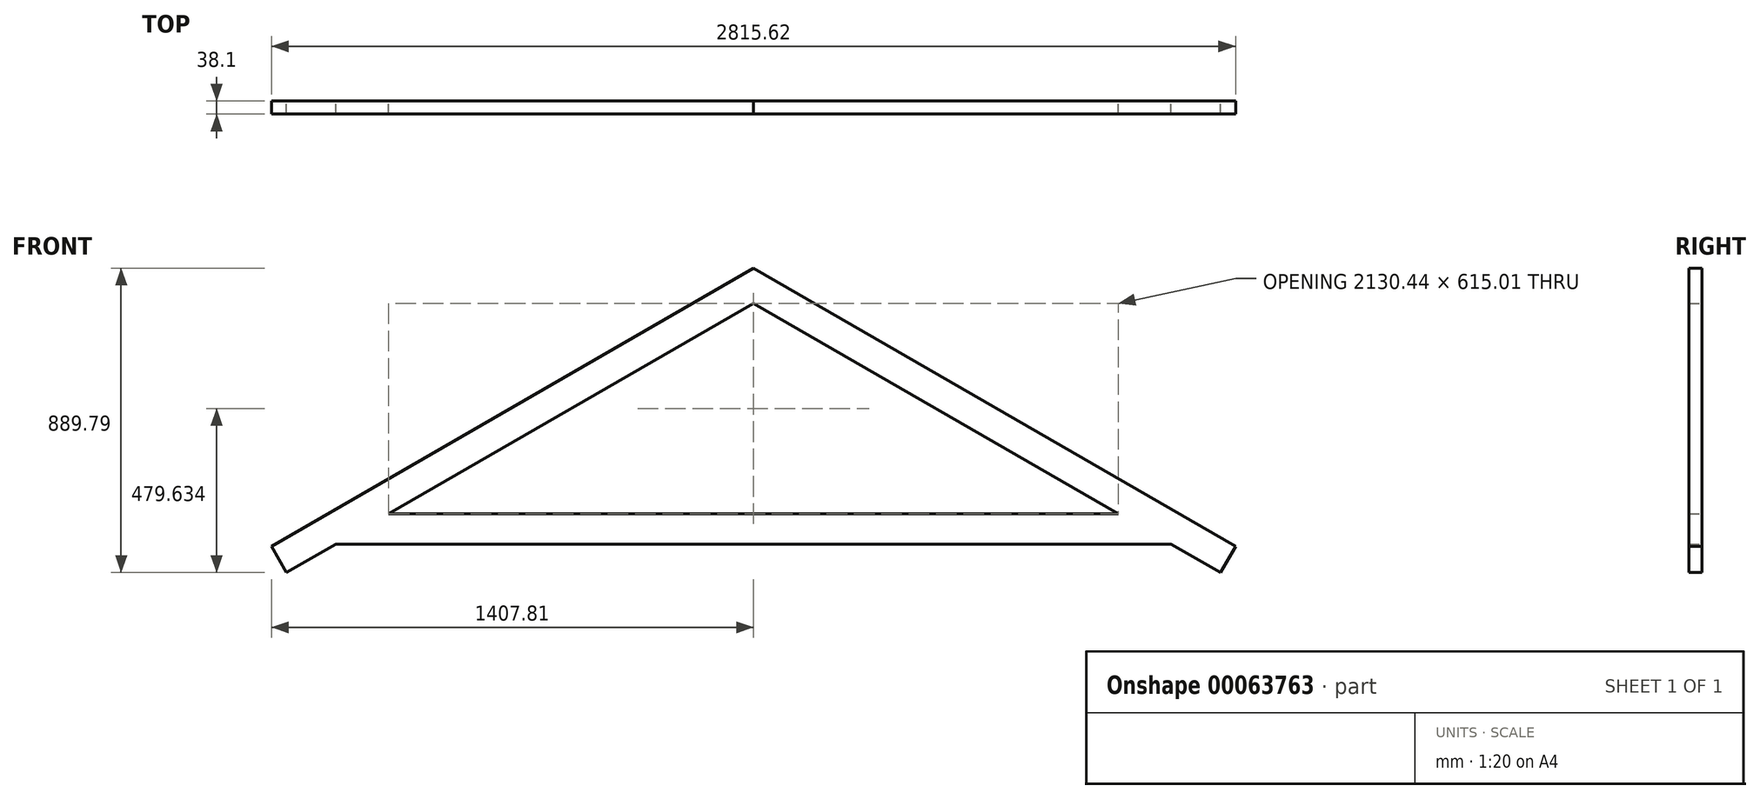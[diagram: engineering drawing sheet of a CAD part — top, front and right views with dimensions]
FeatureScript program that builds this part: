
annotation { "Feature Type Name" : "Feature", "Feature Type Description" : "" }
export const myFeature = defineFeature(function(context is Context, id is Id, definition is map)
    precondition{}
    {
        {
            var Q0;
            Q0=qCreatedBy(makeId("Front.planeOp"),FACE);
            var sketch = newSketch(context, id + "F0", { "sketchPlane" : qUnion([Q0])});
            skLineSegment(sketch, "E0.bottom", {"start": v(-1036.7, -52.67) * mm, "end": v(1093.73, -52.67) * mm});
            skLineSegment(sketch, "E0.top", {"start": v(-1190.69, -141.57) * mm, "end": v(1247.71, -141.57) * mm});
            skLineSegment(sketch, "E1", {"start": v(-1334.85, -224.8) * mm, "end": v(-1190.69, -141.57) * mm});
            skLineSegment(sketch, "E2", {"start": v(1391.87, -224.8) * mm, "end": v(1247.71, -141.57) * mm});
            skLineSegment(sketch, "E3", {"start": v(-1334.85, -224.8) * mm, "end": v(-1379.3, -147.81) * mm});
            skLineSegment(sketch, "E4", {"start": v(-1379.3, -147.81) * mm, "end": v(28.51, 664.99) * mm});
            skLineSegment(sketch, "E5.MirrorCS", {"start": v(1436.32, -147.81) * mm, "end": v(28.51, 664.99) * mm});
            skLineSegment(sketch, "E6.MirrorCS", {"start": v(1391.87, -224.8) * mm, "end": v(1436.32, -147.81) * mm});
            skLineSegment(sketch, "E7.trimOffspring", {"start": v(1093.73, -52.67) * mm, "end": v(28.51, 562.34) * mm});
            skLineSegment(sketch, "E8.trimOffspring", {"start": v(-1036.7, -52.67) * mm, "end": v(28.51, 562.34) * mm});
            skSolve(sketch);
        }
        {
            var Q0;
            Q0 = qSketchRegion(id + "F0", true);
            extrude(context, id + "F1", {"entities" : qUnion([Q0]), "endBound" : BoundingType.SYMMETRIC, "depth" : 38.1 * mm});
        }
    });
